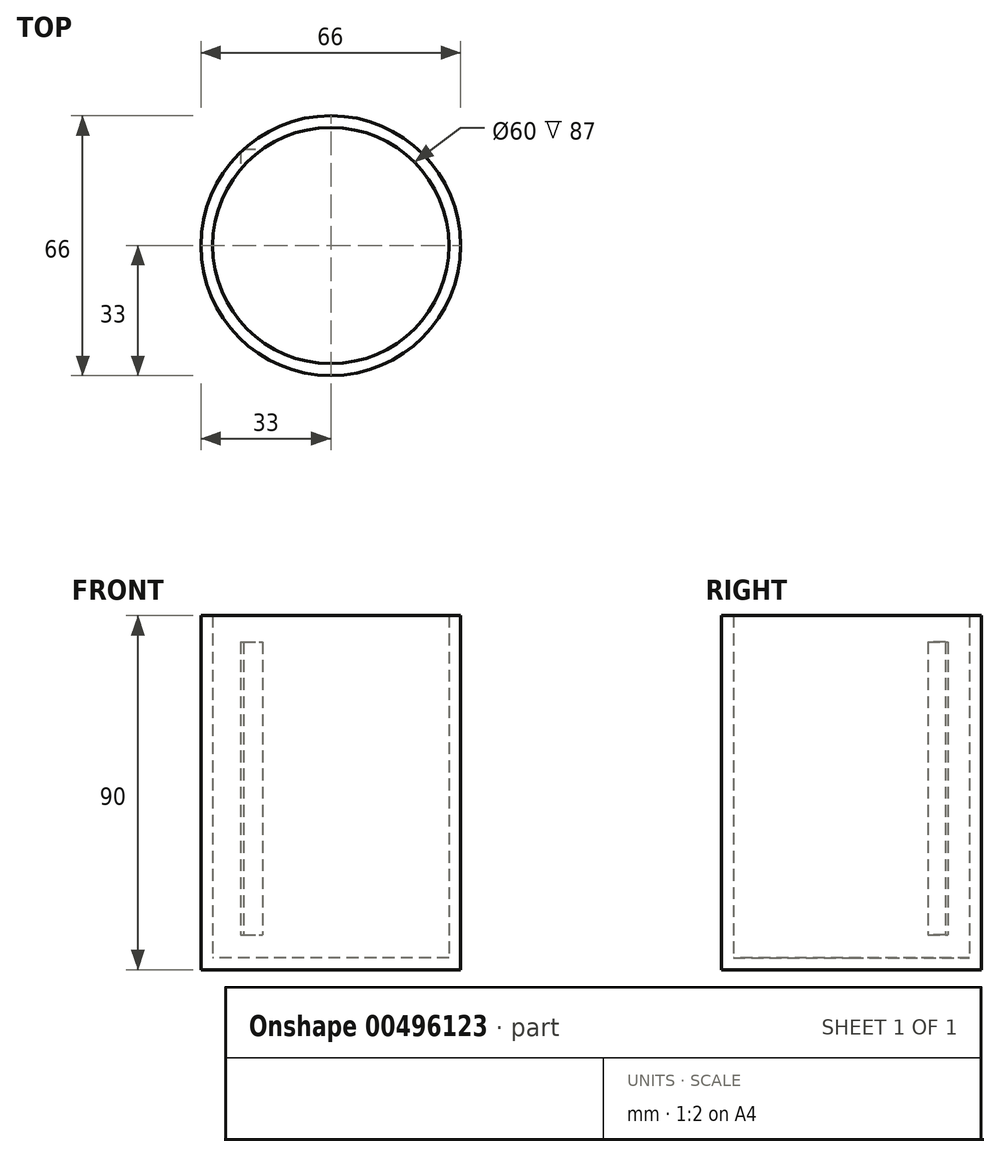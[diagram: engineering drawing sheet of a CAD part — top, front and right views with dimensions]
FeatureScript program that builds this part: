
annotation { "Feature Type Name" : "Feature", "Feature Type Description" : "" }
export const myFeature = defineFeature(function(context is Context, id is Id, definition is map)
    precondition{}
    {
        {
            var Q0;
            Q0=qCreatedBy(makeId("Top.planeOp"),FACE);
            var sketch = newSketch(context, id + "F0", { "sketchPlane" : qUnion([Q0])});
            skCircle(sketch, "E0", {"center": v(0, 0) * mm, "radius": 33 * mm});
            skCircle(sketch, "E1", {"center": v(0, 0) * mm, "radius": 30 * mm});
            skSolve(sketch);
        }
        {
            var Q0;
            Q0=makeQuery(id+"F0.imprint","IMPRINT",FACE,{"disambiguationData":[TD([[makeQuery(id+"F0.imprint","IMPRINT",EDGE,{"derivedFrom":sQuery(id+"F0.wireOp",EDGE,"E1")}),1.0]])]});
            extrude(context, id + "F1", {"entities" : qUnion([Q0]), "depth" : 3 * mm});
        }
        {
            var Q0;
            Q0=qSketchRegion(id+"F0",true);
            extrude(context, id + "F2", {"entities" : qUnion([Q0]), "operationType" : NewBodyOperationType.ADD, "depth" : 90 * mm});
        }
        {
            var Q0;
            Q0=qCreatedBy(makeId("Front.planeOp"),FACE);
            var sketch = newSketch(context, id + "F3", { "sketchPlane" : qUnion([Q0])});
            skLineSegment(sketch, "E2.bottom", {"start": v(-22.85, 83.3) * mm, "end": v(-13.41, 83.3) * mm});
            skLineSegment(sketch, "E2.top", {"start": v(-22.85, 8.93) * mm, "end": v(-13.41, 8.93) * mm});
            skLineSegment(sketch, "E2.left", {"start": v(-22.85, 83.3) * mm, "end": v(-22.85, 8.93) * mm});
            skLineSegment(sketch, "E2.right", {"start": v(-13.41, 83.3) * mm, "end": v(-13.41, 8.93) * mm});
            skSolve(sketch);
        }
        {
            var Q0;
            Q0=makeQuery(id+"F3.imprint","IMPRINT",FACE,{"disambiguationData":[TD([[makeQuery(id+"F3.imprint","IMPRINT",EDGE,{"derivedFrom":sQuery(id+"F3.wireOp",EDGE,"E2.bottom")}),-1.0]])]});
            extrude(context, id + "F4", {"entities" : qUnion([Q0]), "operationType" : NewBodyOperationType.REMOVE, "oppositeDirection" : true, "depth" : 24.5 * mm});
        }
    });
